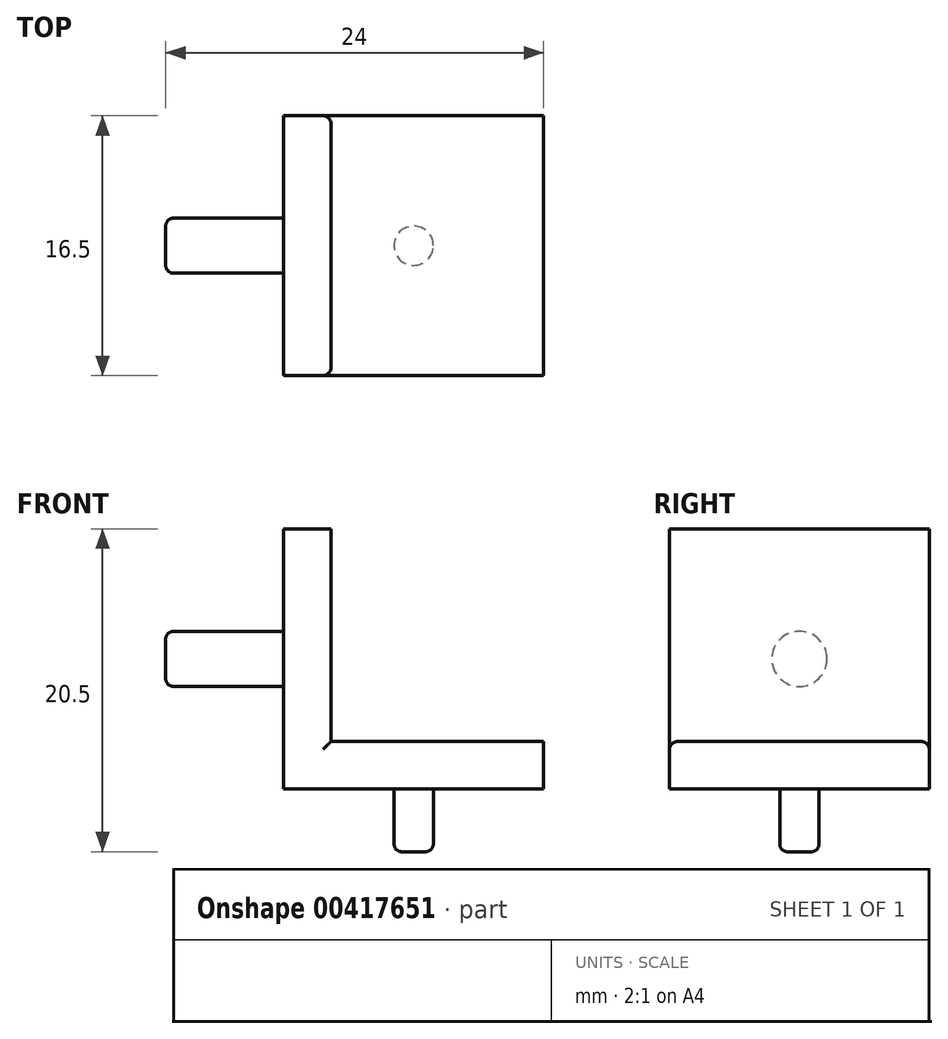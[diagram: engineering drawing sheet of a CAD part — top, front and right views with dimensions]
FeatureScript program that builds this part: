
annotation { "Feature Type Name" : "Feature", "Feature Type Description" : "" }
export const myFeature = defineFeature(function(context is Context, id is Id, definition is map)
    precondition{}
    {
        {
            var Q0;
            Q0=qCreatedBy(makeId("Front.planeOp"),FACE);
            var sketch = newSketch(context, id + "F0", { "sketchPlane" : qUnion([Q0])});
            skLineSegment(sketch, "E0.bottom", {"start": v(0, 3) * mm, "end": v(16.5, 3) * mm});
            skLineSegment(sketch, "E0.top", {"start": v(0, 0) * mm, "end": v(16.5, 0) * mm});
            skLineSegment(sketch, "E0.left", {"start": v(0, 3) * mm, "end": v(0, 0) * mm});
            skLineSegment(sketch, "E0.right", {"start": v(16.5, 3) * mm, "end": v(16.5, 0) * mm});
            skLineSegment(sketch, "E1.bottom", {"start": v(0, 16.5) * mm, "end": v(3, 16.5) * mm});
            skLineSegment(sketch, "E1.top", {"start": v(0, 3) * mm, "end": v(3, 3) * mm});
            skLineSegment(sketch, "E1.left", {"start": v(0, 16.5) * mm, "end": v(0, 3) * mm});
            skLineSegment(sketch, "E1.right", {"start": v(3, 16.5) * mm, "end": v(3, 3) * mm});
            skSolve(sketch);
        }
        {
            var Q0;
            Q0=makeQuery(id+"F0.imprint","IMPRINT",FACE,{"disambiguationData":[TD([[makeQuery(id+"F0.imprint","IMPRINT",EDGE,{"derivedFrom":sQuery(id+"F0.wireOp",EDGE,"E1.bottom")}),-1.0]])]});
            var Q1;
            Q1=makeQuery(id+"F0.imprint","IMPRINT",FACE,{"disambiguationData":[TD([[makeQuery(id+"F0.imprint","IMPRINT",EDGE,{"derivedFrom":sQuery(id+"F0.wireOp",EDGE,"E0.bottom")}),-1.0]])]});
            var Q2;
            Q2 = qSketchRegion(id + "F0", true);
            extrude(context, id + "F1", {"entities" : qUnion([Q0, Q1, Q2]), "depth" : 16.5 * mm});
        }
        {
            var Q0;
            Q0=makeQuery(id+"F1.opExtrude","SWEPT_FACE",FACE,{"disambiguationData":[OSD([sQuery(id+"F0.wireOp",EDGE,"E0.top")])]});
            var sketch = newSketch(context, id + "F2", { "sketchPlane" : qUnion([Q0])});
            skCircle(sketch, "E2", {"center": v(8.25, 8.25) * mm, "radius": 1.25 * mm});
            skPoint(sketch, "E2.centerSnap0", {"position": v(8.25, 16.5) * mm});
            skPoint(sketch, "E2.centerSnap1", {"position": v(0, 8.25) * mm});
            skSolve(sketch);
        }
        {
            var Q0;
            Q0 = qSketchRegion(id + "F2", true);
            extrude(context, id + "F3", {"entities" : qUnion([Q0]), "operationType" : NewBodyOperationType.ADD, "depth" : 4 * mm});
        }
        {
            var Q0;
            Q0=makeQuery(id+"F1.opExtrude","SWEPT_FACE",FACE,{"disambiguationData":[OSD([sQuery(id+"F0.wireOp",EDGE,"E0.left"),sQuery(id+"F0.wireOp",EDGE,"E1.left")])]});
            var sketch = newSketch(context, id + "F4", { "sketchPlane" : qUnion([Q0])});
            skCircle(sketch, "E3", {"center": v(8.25, 8.25) * mm, "radius": 1.75 * mm});
            skPoint(sketch, "E3.centerSnap0", {"position": v(8.25, 16.5) * mm});
            skPoint(sketch, "E3.centerSnap1", {"position": v(0, 8.25) * mm});
            skSolve(sketch);
        }
        {
            var Q0;
            Q0 = qSketchRegion(id + "F4", true);
            extrude(context, id + "F5", {"entities" : qUnion([Q0]), "operationType" : NewBodyOperationType.ADD, "depth" : 7.5 * mm});
        }
        {
            var Q0;
            Q0=makeQuery(id+"F3.opExtrude","CAP_EDGE",EDGE,{"disambiguationData":[OSD([sQuery(id+"F2.wireOp",EDGE,"E2")])],"isStart":false});
            fillet(context, id + "F6", {"entities" : qUnion([Q0]), "radius" : 0.5 * mm, "tangentPropagation" : true, "allowEdgeOverflow" : false});
        }
        {
            var Q0;
            Q0=makeQuery(id+"F5.opExtrude","CAP_EDGE",EDGE,{"disambiguationData":[OSD([sQuery(id+"F4.wireOp",EDGE,"E3")])],"isStart":false});
            fillet(context, id + "F7", {"entities" : qUnion([Q0]), "radius" : .5 * mm, "tangentPropagation" : true, "allowEdgeOverflow" : false});
        }
        {
            var Q0;
            Q0=makeQuery(id+"F1.opExtrude","CAP_EDGE",EDGE,{"disambiguationData":[OSD([sQuery(id+"F0.wireOp",EDGE,"E1.right")])],"isStart":true});
            var Q1;
            Q1=makeQuery(id+"F1.opExtrude","CAP_EDGE",EDGE,{"disambiguationData":[OSD([sQuery(id+"F0.wireOp",EDGE,"E1.right")])],"isStart":false});
            var Q2;
            Q2=makeQuery(id+"F1.opExtrude","CAP_EDGE",EDGE,{"disambiguationData":[OSD([sQuery(id+"F0.wireOp",EDGE,"E0.bottom")])],"isStart":false});
            var Q3;
            Q3=makeQuery(id+"F1.opExtrude","CAP_EDGE",EDGE,{"disambiguationData":[OSD([sQuery(id+"F0.wireOp",EDGE,"E0.bottom")])],"isStart":true});
            fillet(context, id + "F8", {"entities" : qUnion([Q0, Q1, Q2, Q3]), "radius" : 0.5 * mm, "tangentPropagation" : true, "allowEdgeOverflow" : false});
        }
    });
